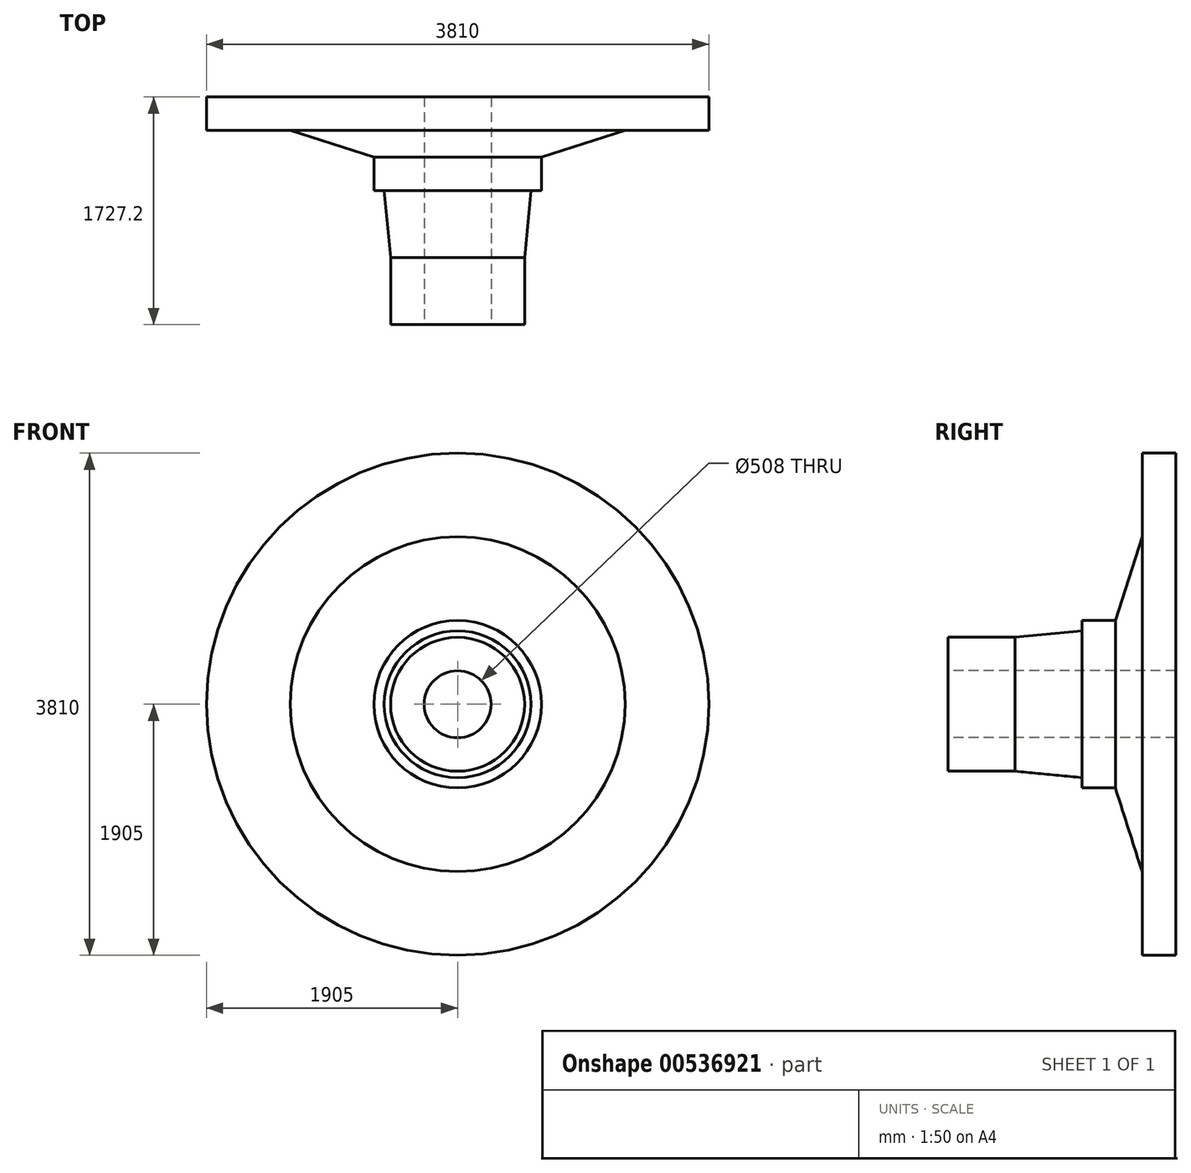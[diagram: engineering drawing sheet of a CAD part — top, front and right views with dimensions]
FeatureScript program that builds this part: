
annotation { "Feature Type Name" : "Feature", "Feature Type Description" : "" }
export const myFeature = defineFeature(function(context is Context, id is Id, definition is map)
    precondition{}
    {
        {
            var Q0;
            Q0=qCreatedBy(makeId("Right.planeOp"),FACE);
            var sketch = newSketch(context, id + "F0", { "sketchPlane" : qUnion([Q0])});
            skLineSegment(sketch, "E0", {"start": v(508, 508) * mm, "end": v(0, 508) * mm});
            skLineSegment(sketch, "E1", {"start": v(0, 508) * mm, "end": v(0, 254) * mm});
            skLineSegment(sketch, "E2", {"start": v(1473.2, 1270) * mm, "end": v(1473.2, 1905) * mm});
            skLineSegment(sketch, "E3", {"start": v(1473.2, 1905) * mm, "end": v(1727.2, 1905) * mm});
            skLineSegment(sketch, "E4", {"start": v(1727.2, 1905) * mm, "end": v(1727.2, 254) * mm});
            skLineSegment(sketch, "E5", {"start": v(1016, 635) * mm, "end": v(1270, 635) * mm});
            skLineSegment(sketch, "E6", {"start": v(1270, 635) * mm, "end": v(1473.2, 1270) * mm});
            skLineSegment(sketch, "E7", {"start": v(508, 508) * mm, "end": v(1016, 557.05) * mm});
            skLineSegment(sketch, "E8.trimOffspring", {"start": v(1016, 557.05) * mm, "end": v(1016, 635) * mm});
            skLineSegment(sketch, "E9", {"start": v(0, 0) * mm, "end": v(1727.2, 0) * mm});
            skLineSegment(sketch, "E10", {"start": v(0, 254) * mm, "end": v(1727.2, 254) * mm});
            skSolve(sketch);
        }
        {
            var Q0;
            Q0=makeQuery(id+"F0.imprint","IMPRINT",FACE,{"disambiguationData":[TD([[makeQuery(id+"F0.imprint","IMPRINT",EDGE,{"derivedFrom":sQuery(id+"F0.wireOp",EDGE,"E0")}),1.0]])]});
            var Q1;
            Q1=sQuery(id+"F0.wireOp",EDGE,"E9");
            revolve(context, id + "F1", {"entities" : qUnion([Q0]), "axis" : qUnion([Q1]), "revolveType" : RevolveType.FULL});
        }
    });
